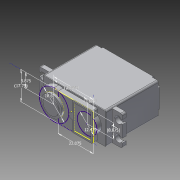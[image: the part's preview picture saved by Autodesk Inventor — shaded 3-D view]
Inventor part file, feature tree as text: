
AUTODESK INVENTOR PART (.ipt)
format: ipt  version: 2015 (Build 190159000, 159)  size: 272,896 bytes
history: native  units: in
note: dims shown in document units (in); Inventor stores cm internally (conversion verified against a paired STEP export)
features: projected_geometry x4, other x3, direct_edit x1, sketch x1, imported_body x1
ambient origin geometry x8: Origin, YZ Plane, XZ Plane, XY Plane, X Axis, Y Axis, Z Axis, Center Point
bodies: Solid1 (feature_tree)
feature tree (10):
  other  "SW3dPS-Hitec Servo.SAT1"
  other  "Move Face1"
  direct_edit  "Direct Edit1"
  sketch  "Sketch1"  dims[d0=0.7323in d1=0.9785in d2=0.3494in d3=0.4893in d4=0.3494in d5=0.1517in d6=0.8268in d7=0.6988in d8=0.8691in d9=0.3939in]
  imported_body  "Base1"
  projected_geometry  "Projected Loop1"
  projected_geometry  "Projected Loop2"
  projected_geometry  "Projected Loop3"
  projected_geometry  "Projected Loop4"
  other  "Delete1"
